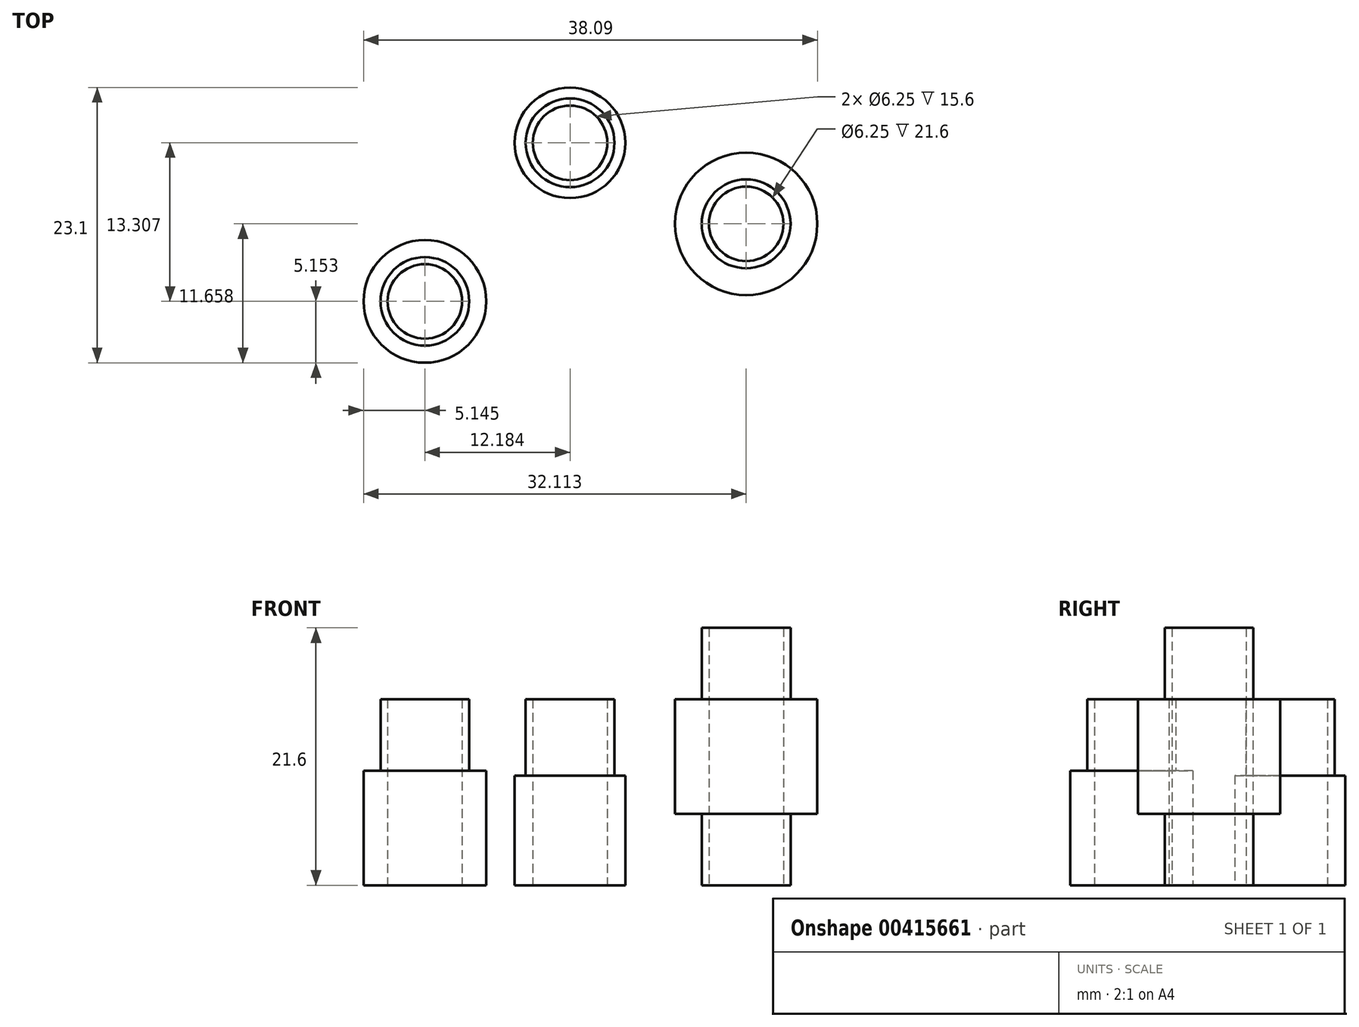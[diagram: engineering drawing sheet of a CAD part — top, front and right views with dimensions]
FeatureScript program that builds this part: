
annotation { "Feature Type Name" : "Feature", "Feature Type Description" : "" }
export const myFeature = defineFeature(function(context is Context, id is Id, definition is map)
    precondition{}
    {
        {
            var Q0;
            Q0=qCreatedBy(makeId("Top.planeOp"),FACE);
            var sketch = newSketch(context, id + "F0", { "sketchPlane" : qUnion([Q0])});
            skCircle(sketch, "E0", {"center": v(0, 0) * mm, "radius": 4.64 * mm});
            skCircle(sketch, "E1", {"center": v(0, 0) * mm, "radius": 3.73 * mm});
            skCircle(sketch, "E2", {"center": v(0, 0) * mm, "radius": 3.12 * mm});
            skSolve(sketch);
        }
        {
            var Q0;
            Q0=makeQuery(id+"F0.imprint","IMPRINT",FACE,{"disambiguationData":[TD([[makeQuery(id+"F0.imprint","IMPRINT",EDGE,{"derivedFrom":sQuery(id+"F0.wireOp",EDGE,"E1")}),1.0]])]});
            extrude(context, id + "F1", {"entities" : qUnion([Q0]), "depth" : 15.6 * mm});
        }
        {
            var Q0;
            Q0=makeQuery(id+"F0.imprint","IMPRINT",FACE,{"disambiguationData":[TD([[makeQuery(id+"F0.imprint","IMPRINT",EDGE,{"derivedFrom":sQuery(id+"F0.wireOp",EDGE,"E0")}),1.0]])]});
            extrude(context, id + "F2", {"entities" : qUnion([Q0]), "operationType" : NewBodyOperationType.ADD, "depth" : 9.2 * mm});
        }
        {
            var Q0;
            Q0=qCreatedBy(makeId("Top.planeOp"),FACE);
            var sketch = newSketch(context, id + "F3", { "sketchPlane" : qUnion([Q0])});
            skCircle(sketch, "E3", {"center": v(14.78, -6.8) * mm, "radius": 5.97 * mm});
            skCircle(sketch, "E4", {"center": v(14.78, -6.8) * mm, "radius": 3.73 * mm});
            skCircle(sketch, "E5", {"center": v(14.78, -6.8) * mm, "radius": 3.12 * mm});
            skSolve(sketch);
        }
        {
            var Q0;
            Q0=makeQuery(id+"F3.imprint","IMPRINT",FACE,{"disambiguationData":[TD([[makeQuery(id+"F3.imprint","IMPRINT",EDGE,{"derivedFrom":sQuery(id+"F3.wireOp",EDGE,"E4")}),1.0]])]});
            extrude(context, id + "F4", {"entities" : qUnion([Q0]), "endBound" : BoundingType.SYMMETRIC, "depth" : 21.6 * mm});
        }
        {
            var Q0;
            Q0=makeQuery(id+"F3.imprint","IMPRINT",FACE,{"disambiguationData":[TD([[makeQuery(id+"F3.imprint","IMPRINT",EDGE,{"derivedFrom":sQuery(id+"F3.wireOp",EDGE,"E3")}),1.0]])]});
            extrude(context, id + "F5", {"entities" : qUnion([Q0]), "operationType" : NewBodyOperationType.ADD, "endBound" : BoundingType.SYMMETRIC, "depth" : 9.6 * mm});
        }
        {
            var Q0;
            Q0=makeQuery(id+"F4.opExtrude","SWEPT_BODY",BODY,{"disambiguationData":[OSD([sQuery(id+"F3.wireOp",EDGE,"E4"),sQuery(id+"F3.wireOp",EDGE,"E5")])]});
            transform(context, id + "F6", {"entities" : qUnion([Q0]), "transformType" : TransformType.TRANSLATION_3D, "dx" : 0 * mm, "dy" : 0 * mm, "dz" : 10.8 * mm, "makeCopy" : false});
        }
        {
            var Q0;
            Q0=qCreatedBy(makeId("Top.planeOp"),FACE);
            var sketch = newSketch(context, id + "F7", { "sketchPlane" : qUnion([Q0])});
            skCircle(sketch, "E6", {"center": v(-12.18, -13.3) * mm, "radius": 5.15 * mm});
            skCircle(sketch, "E7", {"center": v(-12.18, -13.3) * mm, "radius": 3.71 * mm});
            skCircle(sketch, "E8", {"center": v(-12.18, -13.3) * mm, "radius": 3.12 * mm});
            skSolve(sketch);
        }
        {
            var Q0;
            Q0=makeQuery(id+"F7.imprint","IMPRINT",FACE,{"disambiguationData":[TD([[makeQuery(id+"F7.imprint","IMPRINT",EDGE,{"derivedFrom":sQuery(id+"F7.wireOp",EDGE,"E7")}),1.0]])]});
            extrude(context, id + "F8", {"entities" : qUnion([Q0]), "depth" : 15.6 * mm});
        }
        {
            var Q0;
            Q0=makeQuery(id+"F7.imprint","IMPRINT",FACE,{"disambiguationData":[TD([[makeQuery(id+"F7.imprint","IMPRINT",EDGE,{"derivedFrom":sQuery(id+"F7.wireOp",EDGE,"E6")}),1.0]])]});
            extrude(context, id + "F9", {"entities" : qUnion([Q0]), "operationType" : NewBodyOperationType.ADD, "depth" : 9.6 * mm});
        }
    });
